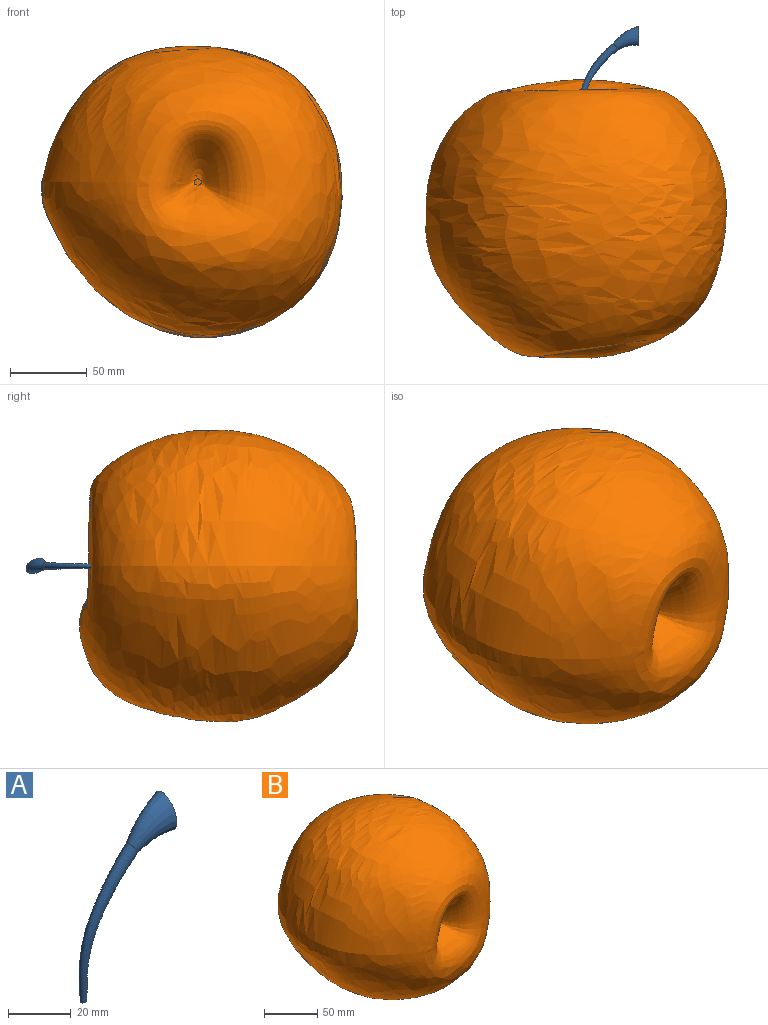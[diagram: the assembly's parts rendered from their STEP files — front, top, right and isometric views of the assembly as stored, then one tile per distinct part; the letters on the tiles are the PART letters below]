
ASSEMBLY  parts=2 mates=1
PART A: 4 faces, bbox 38.9x10x62.4 mm
  f0: plane 2.5x1.69mm, normal (0,0,-1), area 3.3mm2, adj f1
  f1: bspline ~51.26x25.5mm, area 625.5mm2, adj f0,f3
  f2: plane 12.72x10.01mm, normal (1,0,0), area 94.1mm2, adj f3
  f3: bspline ~16.62x15.38mm, area 431.6mm2, adj f1,f2
PART B: 3 faces, bbox 196.9x182.4x190.9 mm
  f0: plane 5.17x4.24mm, normal (0,-1,0), area 15.4mm2, adj f2
  f1: plane 5.17x4.24mm, normal (0,1,0), area 15.4mm2, adj f2
  f2: bspline ~196.66x190.63mm, area 123054.6mm2, adj f0,f1
PLACE A rot(axis=(-1,0,0),90deg) t=(-52.91,47.24,29.92)mm
PLACE B t=(-53.13,-47.75,30.03)mm
MATE fastened A.f0 <-> B.f1  axis (0,-1,0) through (-52.91,47.24,29.92)mm
